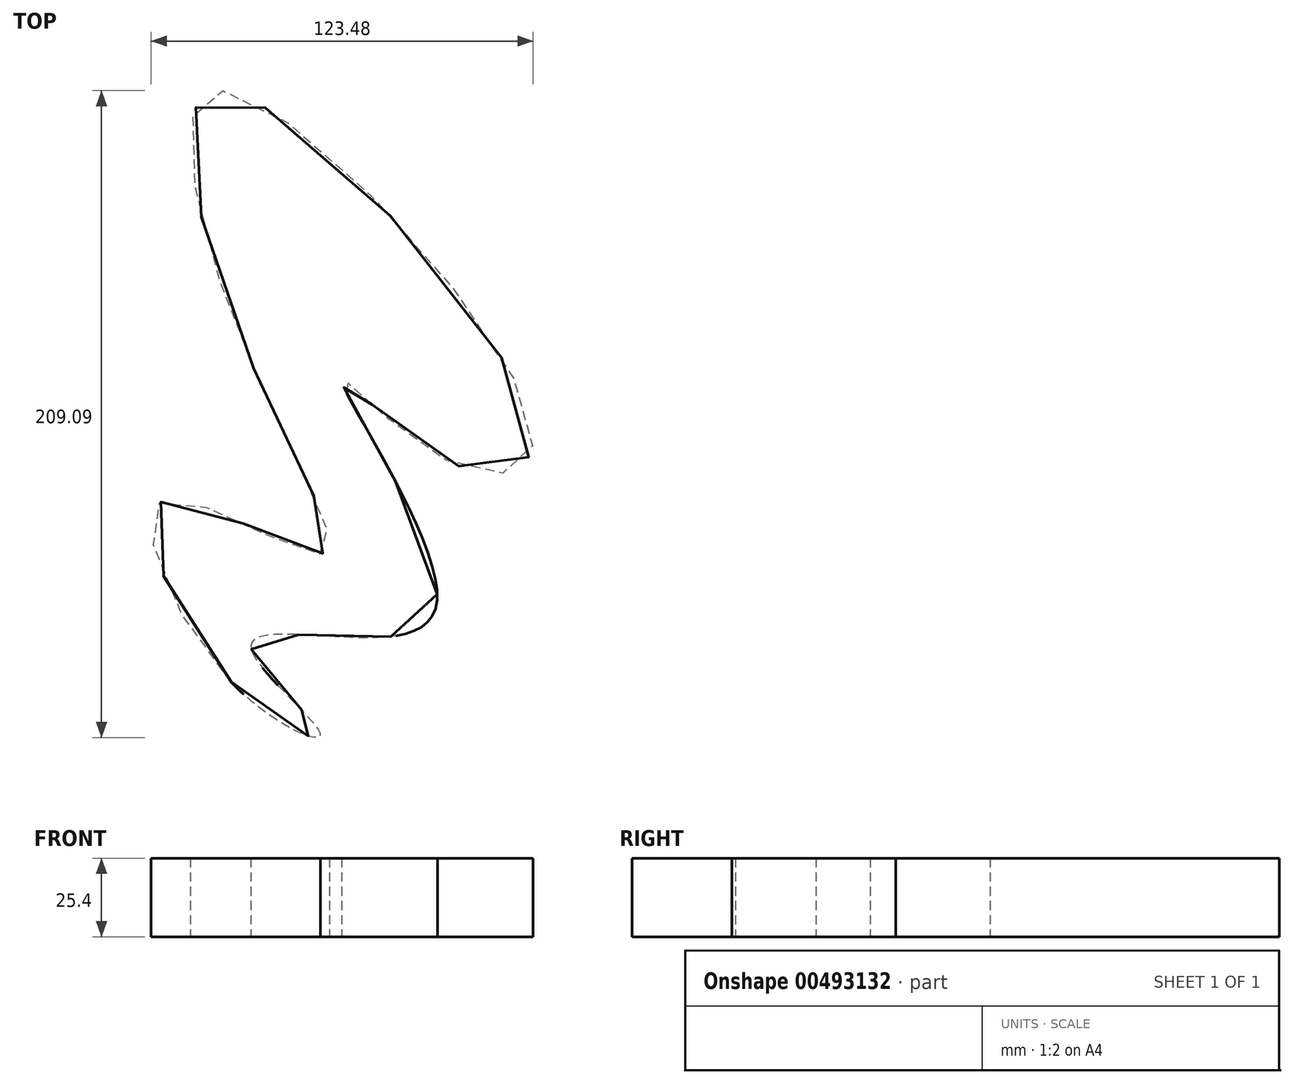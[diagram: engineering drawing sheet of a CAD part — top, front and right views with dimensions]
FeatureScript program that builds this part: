
annotation { "Feature Type Name" : "Feature", "Feature Type Description" : "" }
export const myFeature = defineFeature(function(context is Context, id is Id, definition is map)
    precondition{}
    {
        {
            var Q0;
            Q0=qCreatedBy(makeId("Top.planeOp"),FACE);
            var sketch = newSketch(context, id + "F0", { "sketchPlane" : qUnion([Q0])});
            skFitSpline(sketch, "E0", {"points": [v(-97.6, -52.66) * mm, v(-119.57, 5.86) * mm, v(-68.65, -11.21) * mm, v(-93, 55.1) * mm, v(-101.05, 138.5) * mm, v(0, 27.29) * mm, v(-24.52, 17.3) * mm, v(-61.91, 44.77) * mm, v(-30.97, -25.89) * mm, v(-63.46, -38.06) * mm, v(-91.14, -41.52) * mm, v(-68.84, -69.23) * mm, v(-97.6, -52.66) * mm]});
            skSolve(sketch);
        }
        {
            var Q0;
            Q0=makeQuery(id+"F0.imprint","IMPRINT",FACE,{"disambiguationData":[TD([[makeQuery(id+"F0.imprint","IMPRINT",EDGE,{"derivedFrom":sQuery(id+"F0.wireOp",EDGE,"E0")}),-1.0]])]});
            extrude(context, id + "F1", {"entities" : qUnion([Q0]), "depth" : 25.4 * mm});
        }
    });
